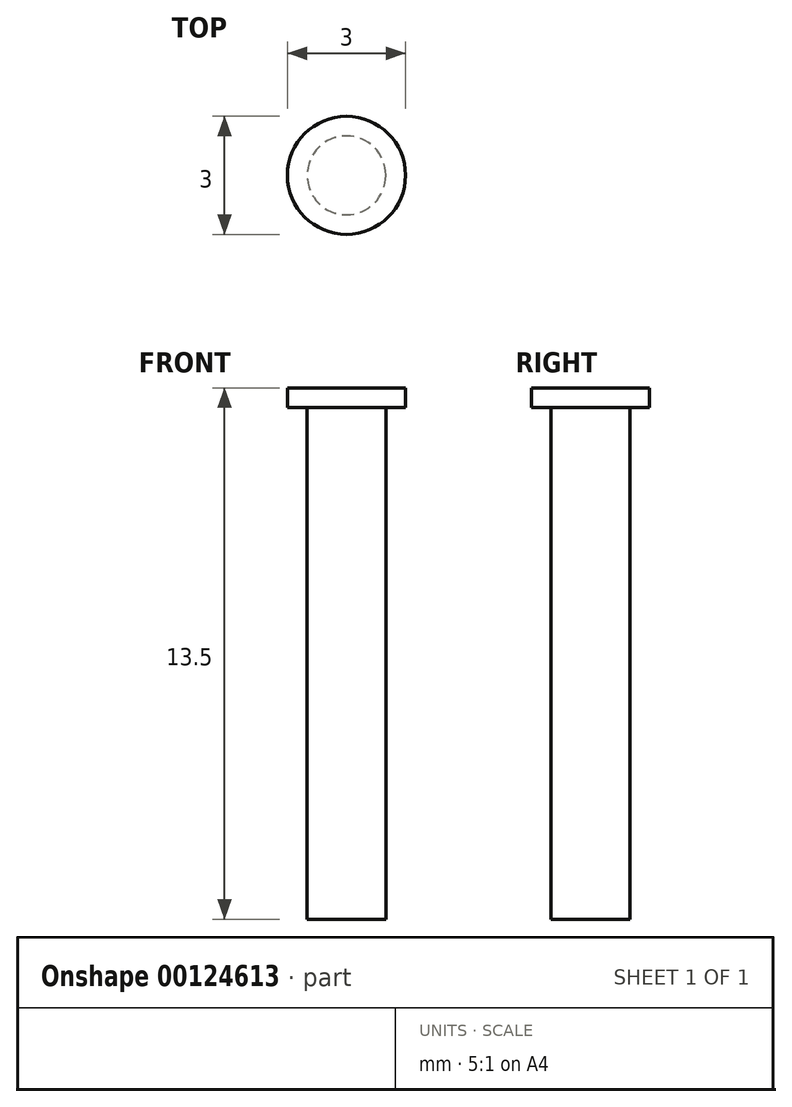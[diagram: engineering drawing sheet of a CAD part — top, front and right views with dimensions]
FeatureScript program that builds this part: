
annotation { "Feature Type Name" : "Feature", "Feature Type Description" : "" }
export const myFeature = defineFeature(function(context is Context, id is Id, definition is map)
    precondition{}
    {
        {
            var Q0;
            Q0=qCreatedBy(makeId("Top.planeOp"),FACE);
            var sketch = newSketch(context, id + "F0", { "sketchPlane" : qUnion([Q0])});
            skCircle(sketch, "E0", {"center": v(0, 0) * mm, "radius": 1 * mm});
            skSolve(sketch);
        }
        {
            var Q0;
            Q0=makeQuery(id+"F0.imprint","IMPRINT",FACE,{"disambiguationData":[TD([[makeQuery(id+"F0.imprint","IMPRINT",EDGE,{"derivedFrom":sQuery(id+"F0.wireOp",EDGE,"E0")}),1.0]])]});
            extrude(context, id + "F1", {"entities" : qUnion([Q0]), "depth" : 13 * mm});
        }
        {
            var Q0;
            Q0=makeQuery(id+"F1.opExtrude","CAP_FACE",FACE,{"disambiguationData":[OSD([sQuery(id+"F0.wireOp",EDGE,"E0")])],"isStart":false});
            var sketch = newSketch(context, id + "F2", { "sketchPlane" : qUnion([Q0])});
            skCircle(sketch, "E1", {"center": v(0, 0) * mm, "radius": 1.5 * mm});
            skSolve(sketch);
        }
        {
            var Q0;
            Q0=qSketchRegion(id+"F2",true);
            extrude(context, id + "F3", {"entities" : qUnion([Q0]), "operationType" : NewBodyOperationType.ADD, "depth" : 0.5 * mm});
        }
    });
